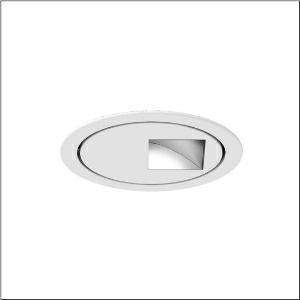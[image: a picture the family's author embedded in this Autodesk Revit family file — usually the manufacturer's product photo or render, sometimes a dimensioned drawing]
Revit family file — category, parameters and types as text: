
# Revit family: lunis_11_mini_round_51dk11cd2wm21
name_source: partatom
category: Lighting Fixtures
units: mm (PartAtom-declared; Revit-internal decimal feet)

## family parameters
Cut with Voids When Loaded = No
Host = Face
Light Source = No
Part Type = Normal
Room Calculation Point = No
Round Connector Dimension = Use Diameter
Shared = No

## types (1)
- Lunis 11 mini round (1 x LED 3000K / CRI = 90 (unbekannt), 1930 lm, 3000K)
    Apparent Load = 28 VA
    CIE Flux Codes = 44 77 97 100 100
    Color Rendering = 90
    Color Temperature = 3000K
    Default Elevation = 1800 mm
    Description = Lunis 11 mini round, downlight, light control with wallwasher, of highly reflective aluminium, highly specular, light emission: direct distribution, LED rated luminous flux: 1.930lm, light colour: 930, control gear: ECG, with terminal, 5-pole, mains connection: 220..230V, AC/DC, 0/50..60Hz, LED module, luminaire module, of aluminium, highly specular, white, diameter: 176mm, clamping range: 1..40mm, recessing ring, of plastic, traffic white (RAL 9016), protection rating (complete): IP20, insulation class (complete): insulation class II (safety insulation), certification: CE, permissible ambient temperature for indoor applications: 0..+35°C, packaging unit: 1 piece
    Height = 0 mm  [stored 0 ft]
    Lamp = 1 x LED 3000K / CRI >= 90 (unbekannt)
    Lamp Light Flux = 1930 lm
    Lamp count = 1
    Length = 176 mm
    Luminous efficacy = 69 lm/W
    Manufacturer = Siteco
    ModVariant = No
    Model = 51DK11CD2WM21
    Mounting Place = Ceiling
    Mounting Type = Recessed
    Number of Poles = 1
    OnlyDefault = Yes
    Power Factor = 1
    Product Name = Lunis 11 mini round
    Product group = downlight
    ProductGroupID = 400
    Protection Class = Protection class II
    Protection Degree = IP 20
    RLX_Detail_Level = 1
    RLX_Emergency_Light_Flux = 0 lm
    RLX_Emergency_Type = 0
    RLX_Emergency_Type_DB = No
    RlxData = <blob elided: 59309 chars, md5=35326d01>
    Socket = socket
    Standby Power = 0 W
    System Light Flux = 1930 lm
    System Power = 28 W
    Type Comments = Product without accessories
    Type Image = l_1004772.jpg
    URL = http://relux.com
    VarID = ---
    Voltage = 0 V
    Weight = 0.00 kg
    Width = 176 mm

note: [stored X ft] marks values corroborated as IEEE doubles in the binary element streams (Revit-internal decimal feet)

## geometry (parser evidence)
native form markers: Blend x4, Sweep x12
no freeform markers — native parametric forms only
